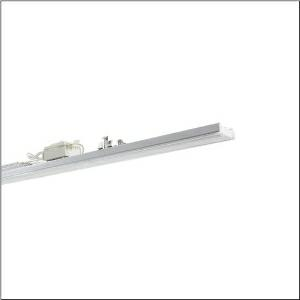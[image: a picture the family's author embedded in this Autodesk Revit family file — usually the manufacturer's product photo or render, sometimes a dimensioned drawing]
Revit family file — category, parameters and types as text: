
# Revit family: licross_11_recessed_mo_51tl18dn495g
name_source: partatom
category: Lighting Fixtures
units: mm (PartAtom-declared; Revit-internal decimal feet)

## family parameters
Cut with Voids When Loaded = No
Host = Face
Light Source = No
Part Type = Normal
Room Calculation Point = No
Round Connector Dimension = Use Diameter
Shared = No

## types (1)
- --- (1 x LED, 9950 lm, 56.7 W, 4000K)
    Apparent Load = 57 VA
    CIE Flux Codes = 83 96 99 100 100
    Color Rendering = 80
    Color Temperature = 4000K
    Default Elevation = 1800 mm
    Description = Licross 11 Recessed MO, luminaire insert, of sheet steel, coil coated, white, length: 1.500mm, width: 66mm, height: 67mm, LED rated luminous flux: 9.950lm, light colour: 840, SDCM (Standard Deviation of Colour Matching)MacAdam ≤ 2 SDCM (initial), control gear: DALI 2, with plug, 5-pole, with phase selection, mains connection: 220..240V, AC, 50/60Hz, rated input power: 57W, internal wiring halogen-free, primary light control with lens, of plastic, primary optical cover: cover, of PMMA, light emission: direct distribution, primary light characteristic: symmetric, protection rating (complete): IP40, insulation class (complete): insulation class I (protective earthing), certification: CE, ENEC, VDE, UKCA, protection symbol: D if used in an environment without relevant dust loads with corresponding accessories, impact resistance: IK06, permissible ambient temperature for indoor applications: -25..+35°C, corresponds to IFS (International Featured Standards) requirements for safety and quality in the food industry, reducing of maximum allowable ambient temperature of 5°C with ceiling mounting, LABS conformity tested according to VDMA 24364:2018-05, The light source and the operating device comply with the requirements of the Ecodesign Regulation (EU) 2019/2020 and are replaceable in accordance with this regulation, packaging unit: 1 piece
    Height = 58 mm
    Lamp = 1 x LED
    Lamp Light Flux = 9950 lm
    Lamp Power = 56.7 W
    Lamp count = 1
    Length = 1500 mm
    Luminous efficacy = 175 lm/W
    Manufacturer = Siteco
    ModVariant = No
    Model = 51TL18DN495G
    Mounting Place = Ceiling
    Mounting Type = Pendant
    Number of Poles = 1
    OnlyDefault = Yes
    Power Factor = 1
    Product Name = Licross 11 Recessed MO
    Product group = luminaire insert | ceiling pendant
    ProductGroupID = 901
    Protection Class = Protection class I
    Protection Degree = IP 40
    RLX_Detail_Level = 1
    RLX_Emergency_Light_Flux = 0 lm
    RLX_Emergency_Type = 0
    RLX_Emergency_Type_DB = No
    RlxData = <blob elided: 24725 chars, md5=6dc83f32>
    Socket = socket
    Standby Power = 0 W
    System Light Flux = 9950 lm
    System Power = 57 W
    Type Comments = factory setting: luminous flux: 100 % | dim-lin: 254 | 378 mA
    Type Image = l_1296930.jpg
    URL = http://relux.com
    VarID = @adj_100735
    Voltage = 0 V
    Weight = 0.00 kg
    Width = 66 mm

## geometry (parser evidence)
native form markers: Blend x4, Sweep x9
no freeform markers — native parametric forms only
